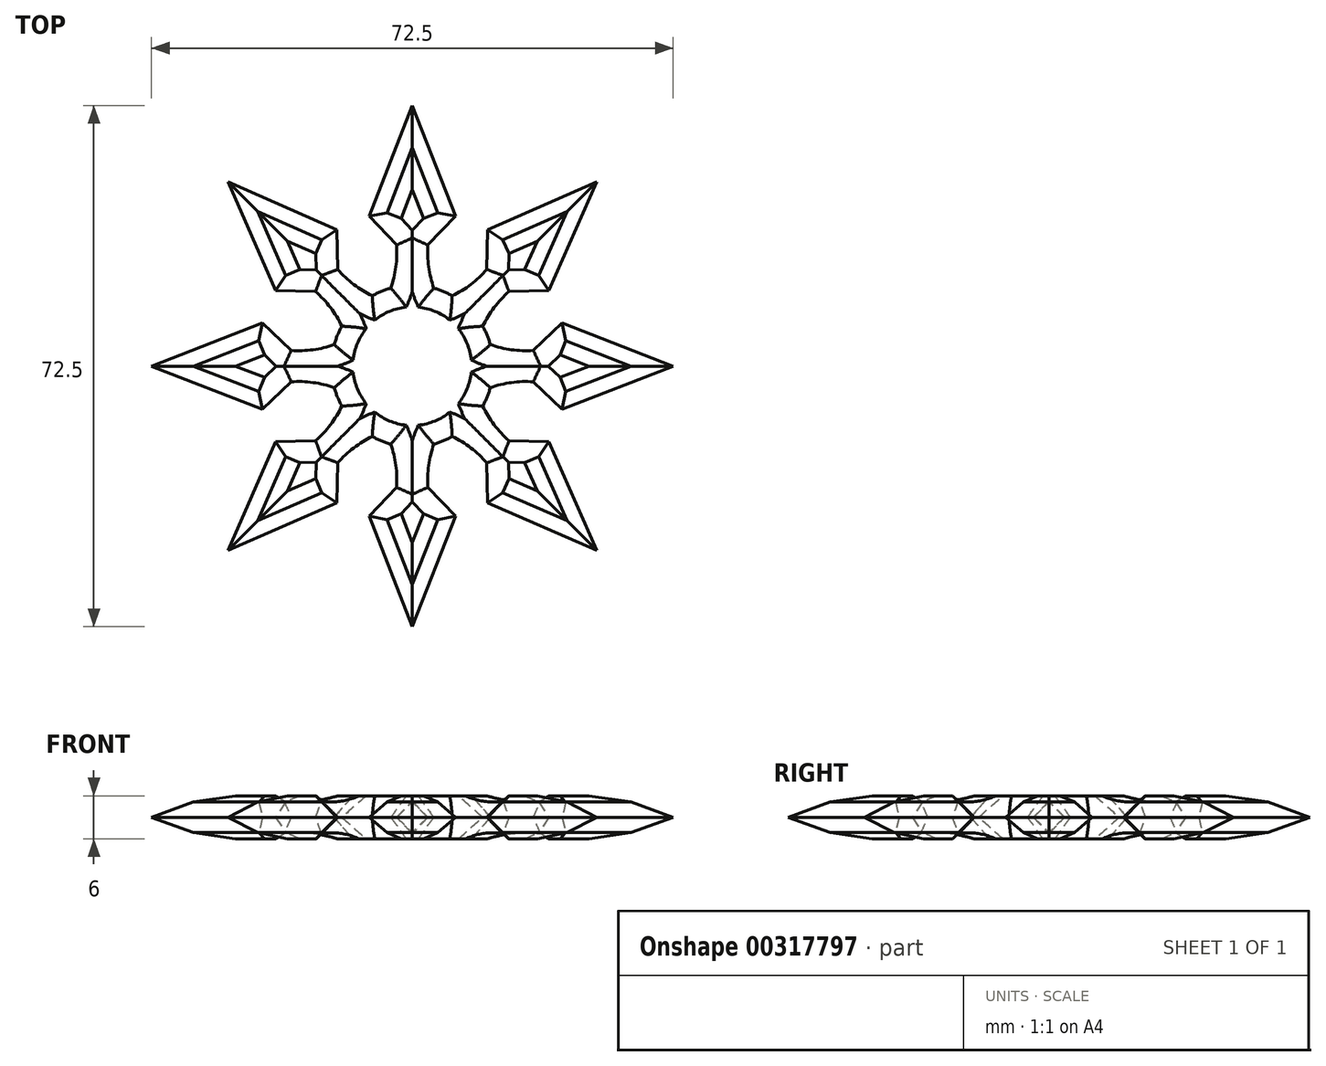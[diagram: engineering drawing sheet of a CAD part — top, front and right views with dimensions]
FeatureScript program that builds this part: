
annotation { "Feature Type Name" : "Feature", "Feature Type Description" : "" }
export const myFeature = defineFeature(function(context is Context, id is Id, definition is map)
    precondition{}
    {
        {
            var Q0;
            Q0=qCreatedBy(makeId("Top.planeOp"),FACE);
            var sketch = newSketch(context, id + "F0", { "sketchPlane" : qUnion([Q0])});
            skCircle(sketch, "E0", {"center": v(0, 0) * mm, "radius": 11.25 * mm});
            skLineSegment(sketch, "E1", {"start": v(0, 0) * mm, "end": v(0, 11.25) * mm, "construction": true});
            skLineSegment(sketch, "E2", {"start": v(0, 0) * mm, "end": v(0, -11.25) * mm, "construction": true});
            skLineSegment(sketch, "E3", {"start": v(0, 0) * mm, "end": v(11.25, 0) * mm, "construction": true});
            skLineSegment(sketch, "E4", {"start": v(0, 0) * mm, "end": v(-11.25, 0) * mm, "construction": true});
            skPoint(sketch, "E5", {"position": v(-3, 10.84) * mm});
            skPoint(sketch, "E6", {"position": v(3, 10.84) * mm});
            skLineSegment(sketch, "E7", {"start": v(-3, 10.84) * mm, "end": v(-3, 20.84) * mm, "construction": true});
            skLineSegment(sketch, "E8", {"start": v(3, 10.84) * mm, "end": v(3, 20.84) * mm, "construction": true});
            skArc(sketch, "E9", {"start": v(-3, 10.84) * mm, "mid": v(-2.14, 15.84) * mm, "end": v(-3, 20.84) * mm});
            skArc(sketch, "E10", {"start": v(3, 20.84) * mm, "mid": v(2.14, 15.84) * mm, "end": v(3, 10.84) * mm});
            skLineSegment(sketch, "E11", {"start": v(3, 20.84) * mm, "end": v(6, 20.84) * mm});
            skLineSegment(sketch, "E12", {"start": v(-3, 20.84) * mm, "end": v(-6, 20.84) * mm});
            skLineSegment(sketch, "E13", {"start": v(0, 36.25) * mm, "end": v(6, 20.84) * mm});
            skLineSegment(sketch, "E14", {"start": v(-6, 20.84) * mm, "end": v(0, 36.25) * mm});
            skPoint(sketch, "E15", {"position": v(2.18, 16.84) * mm});
            skPoint(sketch, "E16", {"position": v(-2.18, 16.84) * mm});
            skLineSegment(sketch, "E17", {"start": v(-6, 20.84) * mm, "end": v(-2.18, 16.84) * mm});
            skLineSegment(sketch, "E18", {"start": v(6, 20.84) * mm, "end": v(2.18, 16.84) * mm});
            skPoint(sketch, "E19.1.0", {"position": v(-13.45, 10.37) * mm});
            skLineSegment(sketch, "E19.1.1", {"start": v(-10.5, 18.98) * mm, "end": v(-10.37, 13.45) * mm});
            skLineSegment(sketch, "E19.1.2", {"start": v(-5.55, 9.79) * mm, "end": v(-12.62, 16.86) * mm, "construction": true});
            skLineSegment(sketch, "E19.1.3", {"start": v(-25.63, 25.63) * mm, "end": v(-10.5, 18.98) * mm});
            skArc(sketch, "E19.1.4", {"start": v(-12.62, 16.86) * mm, "mid": v(-9.69, 12.72) * mm, "end": v(-5.55, 9.79) * mm});
            skPoint(sketch, "E19.1.5", {"position": v(-10.37, 13.45) * mm});
            skLineSegment(sketch, "E19.1.6", {"start": v(-18.98, 10.5) * mm, "end": v(-25.63, 25.63) * mm});
            skLineSegment(sketch, "E19.1.7", {"start": v(-9.79, 5.55) * mm, "end": v(-16.86, 12.62) * mm, "construction": true});
            skLineSegment(sketch, "E19.1.8", {"start": v(-18.98, 10.5) * mm, "end": v(-13.45, 10.37) * mm});
            skArc(sketch, "E19.1.9", {"start": v(-9.79, 5.55) * mm, "mid": v(-12.72, 9.69) * mm, "end": v(-16.86, 12.62) * mm});
            skLineSegment(sketch, "E19.1.10", {"start": v(-16.86, 12.62) * mm, "end": v(-18.98, 10.5) * mm});
            skLineSegment(sketch, "E19.1.11", {"start": v(-12.62, 16.86) * mm, "end": v(-10.5, 18.98) * mm});
            skPoint(sketch, "E19.1.12", {"position": v(-9.79, 5.55) * mm});
            skPoint(sketch, "E19.1.13", {"position": v(-5.55, 9.79) * mm});
            skPoint(sketch, "E19.2.0", {"position": v(-16.84, -2.18) * mm});
            skLineSegment(sketch, "E19.2.1", {"start": v(-20.84, 6) * mm, "end": v(-16.84, 2.18) * mm});
            skLineSegment(sketch, "E19.2.2", {"start": v(-10.84, 3) * mm, "end": v(-20.84, 3) * mm, "construction": true});
            skLineSegment(sketch, "E19.2.3", {"start": v(-36.25, 0) * mm, "end": v(-20.84, 6) * mm});
            skArc(sketch, "E19.2.4", {"start": v(-20.84, 3) * mm, "mid": v(-15.84, 2.14) * mm, "end": v(-10.84, 3) * mm});
            skPoint(sketch, "E19.2.5", {"position": v(-16.84, 2.18) * mm});
            skLineSegment(sketch, "E19.2.6", {"start": v(-20.84, -6) * mm, "end": v(-36.25, 0) * mm});
            skLineSegment(sketch, "E19.2.7", {"start": v(-10.84, -3) * mm, "end": v(-20.84, -3) * mm, "construction": true});
            skLineSegment(sketch, "E19.2.8", {"start": v(-20.84, -6) * mm, "end": v(-16.84, -2.18) * mm});
            skArc(sketch, "E19.2.9", {"start": v(-10.84, -3) * mm, "mid": v(-15.84, -2.14) * mm, "end": v(-20.84, -3) * mm});
            skLineSegment(sketch, "E19.2.10", {"start": v(-20.84, -3) * mm, "end": v(-20.84, -6) * mm});
            skLineSegment(sketch, "E19.2.11", {"start": v(-20.84, 3) * mm, "end": v(-20.84, 6) * mm});
            skPoint(sketch, "E19.2.12", {"position": v(-10.84, -3) * mm});
            skPoint(sketch, "E19.2.13", {"position": v(-10.84, 3) * mm});
            skLineSegment(sketch, "E20.1.3.0", {"start": v(-18.98, -10.5) * mm, "end": v(-13.45, -10.37) * mm});
            skLineSegment(sketch, "E20.4.3.0", {"start": v(-9.79, -5.55) * mm, "end": v(-16.86, -12.62) * mm, "construction": true});
            skLineSegment(sketch, "E20.7.3.0", {"start": v(-25.63, -25.63) * mm, "end": v(-18.98, -10.5) * mm});
            skArc(sketch, "E20.10.3.0", {"start": v(-16.86, -12.62) * mm, "mid": v(-12.72, -9.69) * mm, "end": v(-9.79, -5.55) * mm});
            skPoint(sketch, "E20.14.3.0", {"position": v(-13.45, -10.37) * mm});
            skLineSegment(sketch, "E20.15.3.0", {"start": v(-10.5, -18.98) * mm, "end": v(-25.63, -25.63) * mm});
            skLineSegment(sketch, "E20.18.3.0", {"start": v(-5.55, -9.79) * mm, "end": v(-12.62, -16.86) * mm, "construction": true});
            skLineSegment(sketch, "E20.21.3.0", {"start": v(-10.5, -18.98) * mm, "end": v(-10.37, -13.45) * mm});
            skArc(sketch, "E20.24.3.0", {"start": v(-5.55, -9.79) * mm, "mid": v(-9.69, -12.72) * mm, "end": v(-12.62, -16.86) * mm});
            skPoint(sketch, "E20.25.3.0", {"position": v(-10.37, -13.45) * mm});
            skLineSegment(sketch, "E20.28.3.0", {"start": v(-12.62, -16.86) * mm, "end": v(-10.5, -18.98) * mm});
            skLineSegment(sketch, "E20.31.3.0", {"start": v(-16.86, -12.62) * mm, "end": v(-18.98, -10.5) * mm});
            skPoint(sketch, "E20.34.3.0", {"position": v(-5.55, -9.79) * mm});
            skPoint(sketch, "E20.35.3.0", {"position": v(-9.79, -5.55) * mm});
            skLineSegment(sketch, "E20.1.4.0", {"start": v(-6, -20.84) * mm, "end": v(-2.18, -16.84) * mm});
            skLineSegment(sketch, "E20.4.4.0", {"start": v(-3, -10.84) * mm, "end": v(-3, -20.84) * mm, "construction": true});
            skLineSegment(sketch, "E20.7.4.0", {"start": v(0, -36.25) * mm, "end": v(-6, -20.84) * mm});
            skArc(sketch, "E20.10.4.0", {"start": v(-3, -20.84) * mm, "mid": v(-2.14, -15.84) * mm, "end": v(-3, -10.84) * mm});
            skPoint(sketch, "E20.14.4.0", {"position": v(-2.18, -16.84) * mm});
            skLineSegment(sketch, "E20.15.4.0", {"start": v(6, -20.84) * mm, "end": v(0, -36.25) * mm});
            skLineSegment(sketch, "E20.18.4.0", {"start": v(3, -10.84) * mm, "end": v(3, -20.84) * mm, "construction": true});
            skLineSegment(sketch, "E20.21.4.0", {"start": v(6, -20.84) * mm, "end": v(2.18, -16.84) * mm});
            skArc(sketch, "E20.24.4.0", {"start": v(3, -10.84) * mm, "mid": v(2.14, -15.84) * mm, "end": v(3, -20.84) * mm});
            skPoint(sketch, "E20.25.4.0", {"position": v(2.18, -16.84) * mm});
            skLineSegment(sketch, "E20.28.4.0", {"start": v(3, -20.84) * mm, "end": v(6, -20.84) * mm});
            skLineSegment(sketch, "E20.31.4.0", {"start": v(-3, -20.84) * mm, "end": v(-6, -20.84) * mm});
            skPoint(sketch, "E20.34.4.0", {"position": v(3, -10.84) * mm});
            skPoint(sketch, "E20.35.4.0", {"position": v(-3, -10.84) * mm});
            skLineSegment(sketch, "E20.1.5.0", {"start": v(10.5, -18.98) * mm, "end": v(10.37, -13.45) * mm});
            skLineSegment(sketch, "E20.4.5.0", {"start": v(5.55, -9.79) * mm, "end": v(12.62, -16.86) * mm, "construction": true});
            skLineSegment(sketch, "E20.7.5.0", {"start": v(25.63, -25.63) * mm, "end": v(10.5, -18.98) * mm});
            skArc(sketch, "E20.10.5.0", {"start": v(12.62, -16.86) * mm, "mid": v(9.69, -12.72) * mm, "end": v(5.55, -9.79) * mm});
            skPoint(sketch, "E20.14.5.0", {"position": v(10.37, -13.45) * mm});
            skLineSegment(sketch, "E20.15.5.0", {"start": v(18.98, -10.5) * mm, "end": v(25.63, -25.63) * mm});
            skLineSegment(sketch, "E20.18.5.0", {"start": v(9.79, -5.55) * mm, "end": v(16.86, -12.62) * mm, "construction": true});
            skLineSegment(sketch, "E20.21.5.0", {"start": v(18.98, -10.5) * mm, "end": v(13.45, -10.37) * mm});
            skArc(sketch, "E20.24.5.0", {"start": v(9.79, -5.55) * mm, "mid": v(12.72, -9.69) * mm, "end": v(16.86, -12.62) * mm});
            skPoint(sketch, "E20.25.5.0", {"position": v(13.45, -10.37) * mm});
            skLineSegment(sketch, "E20.28.5.0", {"start": v(16.86, -12.62) * mm, "end": v(18.98, -10.5) * mm});
            skLineSegment(sketch, "E20.31.5.0", {"start": v(12.62, -16.86) * mm, "end": v(10.5, -18.98) * mm});
            skPoint(sketch, "E20.34.5.0", {"position": v(9.79, -5.55) * mm});
            skPoint(sketch, "E20.35.5.0", {"position": v(5.55, -9.79) * mm});
            skLineSegment(sketch, "E21.1.6.0", {"start": v(20.84, -6) * mm, "end": v(16.84, -2.18) * mm});
            skLineSegment(sketch, "E21.4.6.0", {"start": v(10.84, -3) * mm, "end": v(20.84, -3) * mm, "construction": true});
            skLineSegment(sketch, "E21.7.6.0", {"start": v(36.25, 0) * mm, "end": v(20.84, -6) * mm});
            skArc(sketch, "E21.10.6.0", {"start": v(20.84, -3) * mm, "mid": v(15.84, -2.14) * mm, "end": v(10.84, -3) * mm});
            skPoint(sketch, "E21.14.6.0", {"position": v(16.84, -2.18) * mm});
            skLineSegment(sketch, "E21.15.6.0", {"start": v(20.84, 6) * mm, "end": v(36.25, 0) * mm});
            skLineSegment(sketch, "E21.18.6.0", {"start": v(10.84, 3) * mm, "end": v(20.84, 3) * mm, "construction": true});
            skLineSegment(sketch, "E21.21.6.0", {"start": v(20.84, 6) * mm, "end": v(16.84, 2.18) * mm});
            skArc(sketch, "E21.24.6.0", {"start": v(10.84, 3) * mm, "mid": v(15.84, 2.14) * mm, "end": v(20.84, 3) * mm});
            skPoint(sketch, "E21.25.6.0", {"position": v(16.84, 2.18) * mm});
            skLineSegment(sketch, "E21.28.6.0", {"start": v(20.84, 3) * mm, "end": v(20.84, 6) * mm});
            skLineSegment(sketch, "E21.31.6.0", {"start": v(20.84, -3) * mm, "end": v(20.84, -6) * mm});
            skPoint(sketch, "E21.34.6.0", {"position": v(10.84, 3) * mm});
            skPoint(sketch, "E21.35.6.0", {"position": v(10.84, -3) * mm});
            skLineSegment(sketch, "E21.1.7.0", {"start": v(18.98, 10.5) * mm, "end": v(13.45, 10.37) * mm});
            skLineSegment(sketch, "E21.4.7.0", {"start": v(9.79, 5.55) * mm, "end": v(16.86, 12.62) * mm, "construction": true});
            skLineSegment(sketch, "E21.7.7.0", {"start": v(25.63, 25.63) * mm, "end": v(18.98, 10.5) * mm});
            skArc(sketch, "E21.10.7.0", {"start": v(16.86, 12.62) * mm, "mid": v(12.72, 9.69) * mm, "end": v(9.79, 5.55) * mm});
            skPoint(sketch, "E21.14.7.0", {"position": v(13.45, 10.37) * mm});
            skLineSegment(sketch, "E21.15.7.0", {"start": v(10.5, 18.98) * mm, "end": v(25.63, 25.63) * mm});
            skLineSegment(sketch, "E21.18.7.0", {"start": v(5.55, 9.79) * mm, "end": v(12.62, 16.86) * mm, "construction": true});
            skLineSegment(sketch, "E21.21.7.0", {"start": v(10.5, 18.98) * mm, "end": v(10.37, 13.45) * mm});
            skArc(sketch, "E21.24.7.0", {"start": v(5.55, 9.79) * mm, "mid": v(9.69, 12.72) * mm, "end": v(12.62, 16.86) * mm});
            skPoint(sketch, "E21.25.7.0", {"position": v(10.37, 13.45) * mm});
            skLineSegment(sketch, "E21.28.7.0", {"start": v(12.62, 16.86) * mm, "end": v(10.5, 18.98) * mm});
            skLineSegment(sketch, "E21.31.7.0", {"start": v(16.86, 12.62) * mm, "end": v(18.98, 10.5) * mm});
            skPoint(sketch, "E21.34.7.0", {"position": v(5.55, 9.79) * mm});
            skPoint(sketch, "E21.35.7.0", {"position": v(9.79, 5.55) * mm});
            skCircle(sketch, "E22", {"center": v(0, 0) * mm, "radius": 36.25 * mm, "construction": true});
            skSolve(sketch);
        }
        {
            var Q0;
            Q0 = qSketchRegion(id + "F0", true);
            extrude(context, id + "F1", {"entities" : qUnion([Q0]), "depth" : 6 * mm, "offsetDistance" : 25 * mm});
        }
        {
            var Q0;
            Q0=makeQuery(id+"F1.opExtrude","CAP_EDGE",EDGE,{"disambiguationData":[OSD([sQuery(id+"F0.wireOp",EDGE,"E20.15.5.0")])],"isStart":false});
            var Q1;
            Q1=makeQuery(id+"F1.opExtrude","CAP_EDGE",EDGE,{"disambiguationData":[OSD([sQuery(id+"F0.wireOp",EDGE,"E20.7.5.0")])],"isStart":false});
            var Q2;
            Q2=makeQuery(id+"F1.opExtrude","CAP_EDGE",EDGE,{"disambiguationData":[OSD([sQuery(id+"F0.wireOp",EDGE,"E20.15.5.0")])],"isStart":true});
            var Q3;
            Q3=makeQuery(id+"F1.opExtrude","CAP_EDGE",EDGE,{"disambiguationData":[OSD([sQuery(id+"F0.wireOp",EDGE,"E20.7.5.0")])],"isStart":true});
            var Q4;
            Q4=makeQuery(id+"F1.opExtrude","CAP_EDGE",EDGE,{"disambiguationData":[OSD([sQuery(id+"F0.wireOp",EDGE,"E14")])],"isStart":false});
            var Q5;
            Q5=makeQuery(id+"F1.opExtrude","CAP_EDGE",EDGE,{"disambiguationData":[OSD([sQuery(id+"F0.wireOp",EDGE,"E13")])],"isStart":false});
            var Q6;
            Q6=makeQuery(id+"F1.opExtrude","CAP_EDGE",EDGE,{"disambiguationData":[OSD([sQuery(id+"F0.wireOp",EDGE,"E14")])],"isStart":true});
            var Q7;
            Q7=makeQuery(id+"F1.opExtrude","CAP_EDGE",EDGE,{"disambiguationData":[OSD([sQuery(id+"F0.wireOp",EDGE,"E13")])],"isStart":true});
            var Q8;
            Q8=makeQuery(id+"F1.opExtrude","CAP_EDGE",EDGE,{"disambiguationData":[OSD([sQuery(id+"F0.wireOp",EDGE,"E20.7.4.0")])],"isStart":false});
            var Q9;
            Q9=makeQuery(id+"F1.opExtrude","CAP_EDGE",EDGE,{"disambiguationData":[OSD([sQuery(id+"F0.wireOp",EDGE,"E20.15.4.0")])],"isStart":false});
            var Q10;
            Q10=makeQuery(id+"F1.opExtrude","CAP_EDGE",EDGE,{"disambiguationData":[OSD([sQuery(id+"F0.wireOp",EDGE,"E19.1.6")])],"isStart":false});
            var Q11;
            Q11=makeQuery(id+"F1.opExtrude","CAP_EDGE",EDGE,{"disambiguationData":[OSD([sQuery(id+"F0.wireOp",EDGE,"E19.1.3")])],"isStart":false});
            var Q12;
            Q12=makeQuery(id+"F1.opExtrude","CAP_EDGE",EDGE,{"disambiguationData":[OSD([sQuery(id+"F0.wireOp",EDGE,"E19.2.6")])],"isStart":false});
            var Q13;
            Q13=makeQuery(id+"F1.opExtrude","CAP_EDGE",EDGE,{"disambiguationData":[OSD([sQuery(id+"F0.wireOp",EDGE,"E19.2.3")])],"isStart":false});
            var Q14;
            Q14=makeQuery(id+"F1.opExtrude","CAP_EDGE",EDGE,{"disambiguationData":[OSD([sQuery(id+"F0.wireOp",EDGE,"E20.7.3.0")])],"isStart":false});
            var Q15;
            Q15=makeQuery(id+"F1.opExtrude","CAP_EDGE",EDGE,{"disambiguationData":[OSD([sQuery(id+"F0.wireOp",EDGE,"E20.15.3.0")])],"isStart":false});
            var Q16;
            Q16=makeQuery(id+"F1.opExtrude","CAP_EDGE",EDGE,{"disambiguationData":[OSD([sQuery(id+"F0.wireOp",EDGE,"E19.1.6")])],"isStart":true});
            var Q17;
            Q17=makeQuery(id+"F1.opExtrude","CAP_EDGE",EDGE,{"disambiguationData":[OSD([sQuery(id+"F0.wireOp",EDGE,"E19.1.3")])],"isStart":true});
            var Q18;
            Q18=makeQuery(id+"F1.opExtrude","CAP_EDGE",EDGE,{"disambiguationData":[OSD([sQuery(id+"F0.wireOp",EDGE,"E19.2.3")])],"isStart":true});
            var Q19;
            Q19=makeQuery(id+"F1.opExtrude","CAP_EDGE",EDGE,{"disambiguationData":[OSD([sQuery(id+"F0.wireOp",EDGE,"E19.2.6")])],"isStart":true});
            var Q20;
            Q20=makeQuery(id+"F1.opExtrude","CAP_EDGE",EDGE,{"disambiguationData":[OSD([sQuery(id+"F0.wireOp",EDGE,"E20.7.3.0")])],"isStart":true});
            var Q21;
            Q21=makeQuery(id+"F1.opExtrude","CAP_EDGE",EDGE,{"disambiguationData":[OSD([sQuery(id+"F0.wireOp",EDGE,"E20.15.3.0")])],"isStart":true});
            var Q22;
            Q22=makeQuery(id+"F1.opExtrude","CAP_EDGE",EDGE,{"disambiguationData":[OSD([sQuery(id+"F0.wireOp",EDGE,"E20.15.4.0")])],"isStart":true});
            var Q23;
            Q23=makeQuery(id+"F1.opExtrude","CAP_EDGE",EDGE,{"disambiguationData":[OSD([sQuery(id+"F0.wireOp",EDGE,"E20.7.4.0")])],"isStart":true});
            var Q24;
            Q24=makeQuery(id+"F1.opExtrude","CAP_EDGE",EDGE,{"disambiguationData":[OSD([sQuery(id+"F0.wireOp",EDGE,"E21.15.7.0")])],"isStart":false});
            var Q25;
            Q25=makeQuery(id+"F1.opExtrude","CAP_EDGE",EDGE,{"disambiguationData":[OSD([sQuery(id+"F0.wireOp",EDGE,"E21.7.7.0")])],"isStart":false});
            var Q26;
            Q26=makeQuery(id+"F1.opExtrude","CAP_EDGE",EDGE,{"disambiguationData":[OSD([sQuery(id+"F0.wireOp",EDGE,"E21.15.6.0")])],"isStart":false});
            var Q27;
            Q27=makeQuery(id+"F1.opExtrude","CAP_EDGE",EDGE,{"disambiguationData":[OSD([sQuery(id+"F0.wireOp",EDGE,"E21.7.6.0")])],"isStart":false});
            var Q28;
            Q28=makeQuery(id+"F1.opExtrude","CAP_EDGE",EDGE,{"disambiguationData":[OSD([sQuery(id+"F0.wireOp",EDGE,"E21.7.6.0")])],"isStart":true});
            var Q29;
            Q29=makeQuery(id+"F1.opExtrude","CAP_EDGE",EDGE,{"disambiguationData":[OSD([sQuery(id+"F0.wireOp",EDGE,"E21.15.6.0")])],"isStart":true});
            var Q30;
            Q30=makeQuery(id+"F1.opExtrude","CAP_EDGE",EDGE,{"disambiguationData":[OSD([sQuery(id+"F0.wireOp",EDGE,"E21.7.7.0")])],"isStart":true});
            var Q31;
            Q31=makeQuery(id+"F1.opExtrude","CAP_EDGE",EDGE,{"disambiguationData":[OSD([sQuery(id+"F0.wireOp",EDGE,"E21.15.7.0")])],"isStart":true});
            chamfer(context, id + "F2", {"entities" : qUnion([Q0, Q1, Q2, Q3, Q4, Q5, Q6, Q7, Q8, Q9, Q10, Q11, Q12, Q13, Q14, Q15, Q16, Q17, Q18, Q19, Q20, Q21, Q22, Q23, Q24, Q25, Q26, Q27, Q28, Q29, Q30, Q31]), "width" : 3 * mm, "tangentPropagation" : true});
        }
        {
            var Q0;
            Q0=makeQuery(id+"F1.opExtrude","CAP_FACE",FACE,{"disambiguationData":[OSD([sQuery(id+"F0.wireOp",EDGE,"E0"),sQuery(id+"F0.wireOp",EDGE,"E9"),sQuery(id+"F0.wireOp",EDGE,"E10"),sQuery(id+"F0.wireOp",EDGE,"E13"),sQuery(id+"F0.wireOp",EDGE,"E14"),sQuery(id+"F0.wireOp",EDGE,"E17"),sQuery(id+"F0.wireOp",EDGE,"E18"),sQuery(id+"F0.wireOp",EDGE,"E19.1.1"),sQuery(id+"F0.wireOp",EDGE,"E19.1.3"),sQuery(id+"F0.wireOp",EDGE,"E19.1.4"),sQuery(id+"F0.wireOp",EDGE,"E19.1.6"),sQuery(id+"F0.wireOp",EDGE,"E19.1.8"),sQuery(id+"F0.wireOp",EDGE,"E19.1.9"),sQuery(id+"F0.wireOp",EDGE,"E19.2.1"),sQuery(id+"F0.wireOp",EDGE,"E19.2.3"),sQuery(id+"F0.wireOp",EDGE,"E19.2.4"),sQuery(id+"F0.wireOp",EDGE,"E19.2.6"),sQuery(id+"F0.wireOp",EDGE,"E19.2.8"),sQuery(id+"F0.wireOp",EDGE,"E19.2.9"),sQuery(id+"F0.wireOp",EDGE,"E20.1.3.0"),sQuery(id+"F0.wireOp",EDGE,"E20.7.3.0"),sQuery(id+"F0.wireOp",EDGE,"E20.10.3.0"),sQuery(id+"F0.wireOp",EDGE,"E20.15.3.0"),sQuery(id+"F0.wireOp",EDGE,"E20.21.3.0"),sQuery(id+"F0.wireOp",EDGE,"E20.24.3.0"),sQuery(id+"F0.wireOp",EDGE,"E20.1.4.0"),sQuery(id+"F0.wireOp",EDGE,"E20.7.4.0"),sQuery(id+"F0.wireOp",EDGE,"E20.10.4.0"),sQuery(id+"F0.wireOp",EDGE,"E20.15.4.0"),sQuery(id+"F0.wireOp",EDGE,"E20.21.4.0"),sQuery(id+"F0.wireOp",EDGE,"E20.24.4.0"),sQuery(id+"F0.wireOp",EDGE,"E20.1.5.0"),sQuery(id+"F0.wireOp",EDGE,"E20.7.5.0"),sQuery(id+"F0.wireOp",EDGE,"E20.10.5.0"),sQuery(id+"F0.wireOp",EDGE,"E20.15.5.0"),sQuery(id+"F0.wireOp",EDGE,"E20.21.5.0"),sQuery(id+"F0.wireOp",EDGE,"E20.24.5.0"),sQuery(id+"F0.wireOp",EDGE,"E21.1.6.0"),sQuery(id+"F0.wireOp",EDGE,"E21.7.6.0"),sQuery(id+"F0.wireOp",EDGE,"E21.10.6.0"),sQuery(id+"F0.wireOp",EDGE,"E21.15.6.0"),sQuery(id+"F0.wireOp",EDGE,"E21.21.6.0"),sQuery(id+"F0.wireOp",EDGE,"E21.24.6.0"),sQuery(id+"F0.wireOp",EDGE,"E21.1.7.0"),sQuery(id+"F0.wireOp",EDGE,"E21.7.7.0"),sQuery(id+"F0.wireOp",EDGE,"E21.10.7.0"),sQuery(id+"F0.wireOp",EDGE,"E21.15.7.0"),sQuery(id+"F0.wireOp",EDGE,"E21.21.7.0"),sQuery(id+"F0.wireOp",EDGE,"E21.24.7.0")])],"isStart":true});
            var Q1;
            Q1=makeQuery(id+"F1.opExtrude","CAP_FACE",FACE,{"disambiguationData":[OSD([sQuery(id+"F0.wireOp",EDGE,"E0"),sQuery(id+"F0.wireOp",EDGE,"E9"),sQuery(id+"F0.wireOp",EDGE,"E10"),sQuery(id+"F0.wireOp",EDGE,"E13"),sQuery(id+"F0.wireOp",EDGE,"E14"),sQuery(id+"F0.wireOp",EDGE,"E17"),sQuery(id+"F0.wireOp",EDGE,"E18"),sQuery(id+"F0.wireOp",EDGE,"E19.1.1"),sQuery(id+"F0.wireOp",EDGE,"E19.1.3"),sQuery(id+"F0.wireOp",EDGE,"E19.1.4"),sQuery(id+"F0.wireOp",EDGE,"E19.1.6"),sQuery(id+"F0.wireOp",EDGE,"E19.1.8"),sQuery(id+"F0.wireOp",EDGE,"E19.1.9"),sQuery(id+"F0.wireOp",EDGE,"E19.2.1"),sQuery(id+"F0.wireOp",EDGE,"E19.2.3"),sQuery(id+"F0.wireOp",EDGE,"E19.2.4"),sQuery(id+"F0.wireOp",EDGE,"E19.2.6"),sQuery(id+"F0.wireOp",EDGE,"E19.2.8"),sQuery(id+"F0.wireOp",EDGE,"E19.2.9"),sQuery(id+"F0.wireOp",EDGE,"E20.1.3.0"),sQuery(id+"F0.wireOp",EDGE,"E20.7.3.0"),sQuery(id+"F0.wireOp",EDGE,"E20.10.3.0"),sQuery(id+"F0.wireOp",EDGE,"E20.15.3.0"),sQuery(id+"F0.wireOp",EDGE,"E20.21.3.0"),sQuery(id+"F0.wireOp",EDGE,"E20.24.3.0"),sQuery(id+"F0.wireOp",EDGE,"E20.1.4.0"),sQuery(id+"F0.wireOp",EDGE,"E20.7.4.0"),sQuery(id+"F0.wireOp",EDGE,"E20.10.4.0"),sQuery(id+"F0.wireOp",EDGE,"E20.15.4.0"),sQuery(id+"F0.wireOp",EDGE,"E20.21.4.0"),sQuery(id+"F0.wireOp",EDGE,"E20.24.4.0"),sQuery(id+"F0.wireOp",EDGE,"E20.1.5.0"),sQuery(id+"F0.wireOp",EDGE,"E20.7.5.0"),sQuery(id+"F0.wireOp",EDGE,"E20.10.5.0"),sQuery(id+"F0.wireOp",EDGE,"E20.15.5.0"),sQuery(id+"F0.wireOp",EDGE,"E20.21.5.0"),sQuery(id+"F0.wireOp",EDGE,"E20.24.5.0"),sQuery(id+"F0.wireOp",EDGE,"E21.1.6.0"),sQuery(id+"F0.wireOp",EDGE,"E21.7.6.0"),sQuery(id+"F0.wireOp",EDGE,"E21.10.6.0"),sQuery(id+"F0.wireOp",EDGE,"E21.15.6.0"),sQuery(id+"F0.wireOp",EDGE,"E21.21.6.0"),sQuery(id+"F0.wireOp",EDGE,"E21.24.6.0"),sQuery(id+"F0.wireOp",EDGE,"E21.1.7.0"),sQuery(id+"F0.wireOp",EDGE,"E21.7.7.0"),sQuery(id+"F0.wireOp",EDGE,"E21.10.7.0"),sQuery(id+"F0.wireOp",EDGE,"E21.15.7.0"),sQuery(id+"F0.wireOp",EDGE,"E21.21.7.0"),sQuery(id+"F0.wireOp",EDGE,"E21.24.7.0")])],"isStart":false});
            chamfer(context, id + "F3", {"entities" : qUnion([Q0, Q1]), "width" : 3 * mm, "tangentPropagation" : true});
        }
    });
